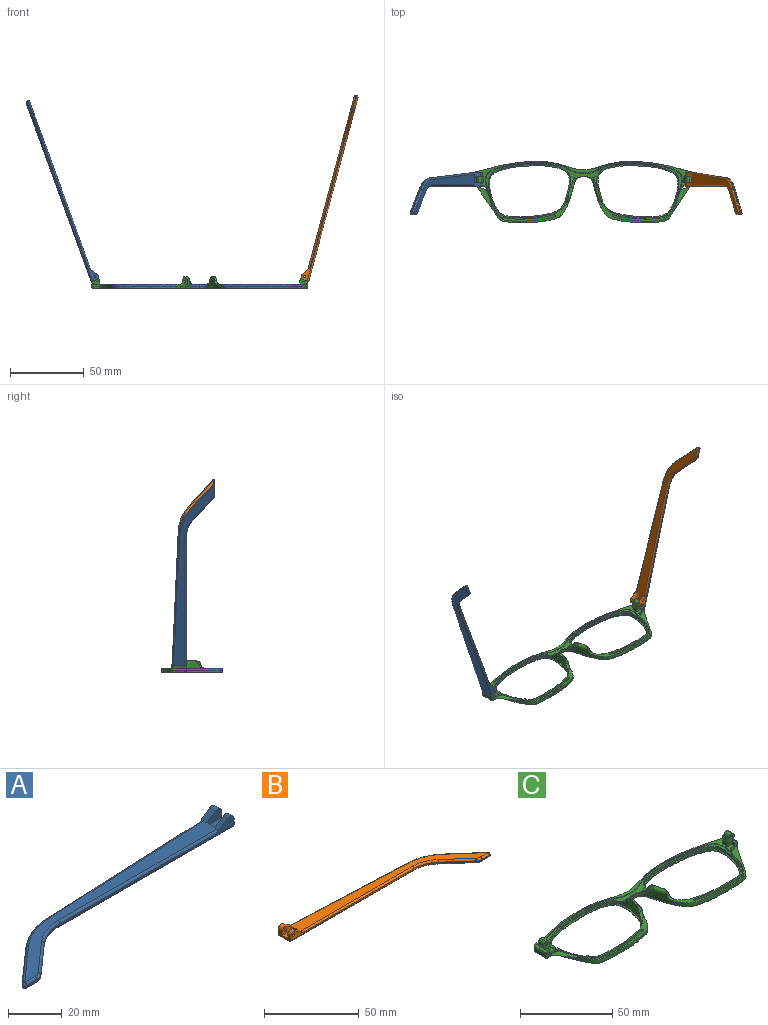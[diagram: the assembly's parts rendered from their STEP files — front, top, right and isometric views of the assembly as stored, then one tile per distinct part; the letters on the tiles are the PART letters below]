
ASSEMBLY  parts=3 mates=2
PART A: 43 faces, bbox 130.2x29.5x5.9 mm
  f0: plane 9.62x3.72mm, normal (1,0,0), area 24.7mm2, adj f1,f3,f4,f5,f10,f16,f18,f28
  f1: cylinder r=2.2mm len=3.45mm, axis (0,-1,0), area 11mm2, adj f0,f2,f4,f37
  f2: plane 6.01x3.91mm, normal (-0.55,0,0.84), area 12.7mm2, adj f1,f4,f9,f19,f37
  f3: plane 2.26x0.1mm, normal (0,0,1), area 0.1mm2, adj f0,f5,f18
  f4: plane 92.1x4.9mm, normal (0,-1,0), area 79.9mm2, adj f0,f1,f2,f14,f19,f36,f42
  f5: plane 93.42x4.13mm, normal (-0.04,1,0), area 64.8mm2, adj f0,f3,f11,f15,f17,f27,f28
  f6: plane 17.82x15.72mm, normal (-0.66,0.75,0), area 14.3mm2, adj f11,f12,f25,f30
  f7: plane 5.46x0.6mm, normal (0,-1,0), area 3.3mm2, adj f12,f13,f23,f32
  f8: plane 14.99x13.23mm, normal (0.66,-0.75,0), area 12mm2, adj f13,f14,f21,f34
  f9: plane 121.18x26.73mm, normal (0,0,1), area 627.7mm2, adj f2,f17,f19,f20,f21,f22,f23,f25
  f10: plane 129.1x27.08mm, normal (0,0,-1), area 686.5mm2, adj f0,f28,f29,f30,f32,f33,f34,f35
  f11: cylinder r=30mm len=18.52mm, axis (0,0,-1), area 12.2mm2, adj f5,f6,f26,f29
  f12: cylinder r=1mm len=1.75mm, axis (0,0,-1), area 1.5mm2, adj f6,f7,f24,f31
  f13: cylinder r=5mm len=3.31mm, axis (0,0,-1), area 2.2mm2, adj f7,f8,f22,f33
  f14: cylinder r=20mm len=13.23mm, axis (0,0,1), area 8.7mm2, adj f4,f8,f20,f35
  f15: plane 5.66x0.25mm, normal (0,0,-1), area 0.7mm2, adj f5,f17,f18
  f16: cylinder r=2.2mm len=3.45mm, axis (0,-1,0), area 14.8mm2, adj f0,f17,f18,f38
  f17: plane 6.01x3.91mm, normal (-0.55,0,0.84), area 16.9mm2, adj f5,f9,f15,f16,f18,f27,f38
  f18: plane 7.92x3.3mm, normal (0,1,0), area 15.9mm2, adj f0,f3,f15,f16,f17,f41
  f19: cylinder r=1mm len=84.18mm, axis (-1,0,0), area 131.4mm2, adj f2,f4,f9,f20
  f20: torus R=21mm, axis (0,0,1), area 23.1mm2, adj f9,f14,f19,f21
  f21: cylinder r=1mm len=15.65mm, axis (-0.75,-0.66,0), area 31.4mm2, adj f8,f9,f20,f22
  f22: torus R=4mm, axis (0,0,1), area 5.3mm2, adj f9,f13,f21,f23
  f23: cylinder r=1mm len=5.46mm, axis (-1,0,0), area 8.6mm2, adj f7,f9,f22,f24
  f24: sphere r=1mm, area 2.4mm2, adj f12,f23,f25
  f25: cylinder r=1mm len=18.48mm, axis (0.75,0.66,0), area 37.3mm2, adj f6,f9,f24,f26
  f26: torus R=29mm, axis (0,0,1), area 31.6mm2, adj f9,f11,f25,f27
  f27: cylinder r=1mm len=85.5mm, axis (1,0.04,0), area 133.5mm2, adj f5,f9,f17,f26
  f28: cylinder r=1mm len=93.46mm, axis (-1,-0.04,0), area 146.9mm2, adj f0,f5,f10,f29
  f29: torus R=29mm, axis (0,0,1), area 31.6mm2, adj f10,f11,f28,f30
  f30: cylinder r=1mm len=18.48mm, axis (-0.75,-0.66,0), area 37.3mm2, adj f6,f10,f29,f31
  f31: sphere r=1mm, area 2.4mm2, adj f12,f30,f32
  f32: cylinder r=1mm len=5.46mm, axis (1,0,0), area 8.6mm2, adj f7,f10,f31,f33
  f33: torus R=4mm, axis (0,0,1), area 5.3mm2, adj f10,f13,f32,f34
  f34: cylinder r=1mm len=15.65mm, axis (0.75,0.66,0), area 31.4mm2, adj f8,f10,f33,f35
  f35: torus R=21mm, axis (0,0,1), area 23.1mm2, adj f10,f14,f34,f36
  f36: cylinder r=1mm len=92.1mm, axis (1,0,0), area 144.7mm2, adj f0,f4,f10,f35
  f37: plane 7.92x4.7mm, normal (0,1,0), area 27mm2, adj f0,f1,f2,f39,f40,f42
  f38: plane 7.92x4.7mm, normal (0,-1,0), area 27mm2, adj f0,f16,f17,f39,f40,f41
  f39: plane 7.92x4.1mm, normal (0,0,1), area 32.5mm2, adj f0,f37,f38,f40
  f40: plane 4.1x1.4mm, normal (1,0,0), area 5.7mm2, adj f9,f37,f38,f39
  f41: cylinder r=0.5mm len=3.1mm, axis (0,-1,0), area 9.7mm2, adj f18,f38
  f42: cylinder r=0.5mm len=2.3mm, axis (0,-1,0), area 7.2mm2, adj f4,f37
PART B: 43 faces, bbox 130.2x29.5x5.9 mm
  f0: plane 9.62x3.72mm, normal (-1,0,0), area 24.7mm2, adj f1,f3,f4,f5,f10,f16,f18,f28
  f1: cylinder r=2.2mm len=3.45mm, axis (0,-1,0), area 11mm2, adj f0,f2,f4,f37
  f2: plane 6.01x3.91mm, normal (0.55,0,0.84), area 12.7mm2, adj f1,f4,f9,f19,f37
  f3: plane 2.26x0.1mm, normal (0,0,1), area 0.1mm2, adj f0,f5,f18
  f4: plane 92.1x4.9mm, normal (0,-1,0), area 78.2mm2, adj f0,f1,f2,f14,f19,f36,f42
  f5: plane 93.42x4.13mm, normal (0.04,1,0), area 64.8mm2, adj f0,f3,f11,f15,f17,f27,f28
  f6: plane 17.82x15.72mm, normal (0.66,0.75,0), area 14.3mm2, adj f11,f12,f25,f30
  f7: plane 5.46x0.6mm, normal (0,-1,0), area 3.3mm2, adj f12,f13,f23,f32
  f8: plane 14.99x13.23mm, normal (-0.66,-0.75,0), area 12mm2, adj f13,f14,f21,f34
  f9: plane 121.18x26.73mm, normal (0,0,1), area 627.7mm2, adj f2,f17,f19,f20,f21,f22,f23,f25
  f10: plane 129.1x27.08mm, normal (0,0,-1), area 686.5mm2, adj f0,f28,f29,f30,f32,f33,f34,f35
  f11: cylinder r=30mm len=18.52mm, axis (0,0,-1), area 12.2mm2, adj f5,f6,f26,f29
  f12: cylinder r=1mm len=1.75mm, axis (0,0,-1), area 1.5mm2, adj f6,f7,f24,f31
  f13: cylinder r=5mm len=3.31mm, axis (0,0,-1), area 2.2mm2, adj f7,f8,f22,f33
  f14: cylinder r=20mm len=13.23mm, axis (0,0,1), area 8.7mm2, adj f4,f8,f20,f35
  f15: plane 5.66x0.25mm, normal (0,0,-1), area 0.7mm2, adj f5,f17,f18
  f16: cylinder r=2.2mm len=3.45mm, axis (0,-1,0), area 14.8mm2, adj f0,f17,f18,f38
  f17: plane 6.01x3.91mm, normal (0.55,0,0.84), area 16.9mm2, adj f5,f9,f15,f16,f18,f27,f38
  f18: plane 7.92x3.3mm, normal (0,1,0), area 14.3mm2, adj f0,f3,f15,f16,f17,f41
  f19: cylinder r=1mm len=84.18mm, axis (1,0,0), area 131.4mm2, adj f2,f4,f9,f20
  f20: torus R=21mm, axis (0,0,1), area 23.1mm2, adj f9,f14,f19,f21
  f21: cylinder r=1mm len=15.65mm, axis (0.75,-0.66,0), area 31.4mm2, adj f8,f9,f20,f22
  f22: torus R=4mm, axis (0,0,1), area 5.3mm2, adj f9,f13,f21,f23
  f23: cylinder r=1mm len=5.46mm, axis (1,0,0), area 8.6mm2, adj f7,f9,f22,f24
  f24: sphere r=1mm, area 2.4mm2, adj f12,f23,f25
  f25: cylinder r=1mm len=18.48mm, axis (-0.75,0.66,0), area 37.3mm2, adj f6,f9,f24,f26
  f26: torus R=29mm, axis (0,0,1), area 31.6mm2, adj f9,f11,f25,f27
  f27: cylinder r=1mm len=85.5mm, axis (-1,0.04,0), area 133.5mm2, adj f5,f9,f17,f26
  f28: cylinder r=1mm len=93.46mm, axis (1,-0.04,0), area 146.9mm2, adj f0,f5,f10,f29
  f29: torus R=29mm, axis (0,0,1), area 31.6mm2, adj f10,f11,f28,f30
  f30: cylinder r=1mm len=18.48mm, axis (0.75,-0.66,0), area 37.3mm2, adj f6,f10,f29,f31
  f31: sphere r=1mm, area 2.4mm2, adj f12,f30,f32
  f32: cylinder r=1mm len=5.46mm, axis (-1,0,0), area 8.6mm2, adj f7,f10,f31,f33
  f33: torus R=4mm, axis (0,0,1), area 5.3mm2, adj f10,f13,f32,f34
  f34: cylinder r=1mm len=15.65mm, axis (-0.75,0.66,0), area 31.4mm2, adj f8,f10,f33,f35
  f35: torus R=21mm, axis (0,0,1), area 23.1mm2, adj f10,f14,f34,f36
  f36: cylinder r=1mm len=92.1mm, axis (-1,0,0), area 144.7mm2, adj f0,f4,f10,f35
  f37: plane 7.92x4.7mm, normal (0,1,0), area 25.4mm2, adj f0,f1,f2,f39,f40,f42
  f38: plane 7.92x4.7mm, normal (0,-1,0), area 25.4mm2, adj f0,f16,f17,f39,f40,f41
  f39: plane 7.92x4.1mm, normal (0,0,1), area 32.5mm2, adj f0,f37,f38,f40
  f40: plane 4.1x1.4mm, normal (-1,0,0), area 5.7mm2, adj f9,f37,f38,f39
  f41: cylinder r=0.88mm len=3.1mm, axis (0,-1,0), area 17mm2, adj f18,f38
  f42: cylinder r=0.88mm len=2.3mm, axis (0,-1,0), area 12.6mm2, adj f4,f37
PART C: 141 faces, bbox 148.1x42.6x10.5 mm
  f0: plane 147.73x42.21mm, normal (0,0,1), area 711.9mm2, adj f4,f5,f6,f7,f8,f12,f20,f23
  f1: bspline ~1.83x1.22mm, area 0.7mm2, adj f2,f7,f37,f52
  f2: bspline ~5.62x4.9mm, area 12.7mm2, adj f1,f7,f37,f41,f43,f52,f53
  f3: plane 4.46x1.43mm, normal (0,0,1), area 0.1mm2, adj f7,f38
  f4: plane 1.23x0.04mm, normal (0,0,1), area 0mm2, adj f0,f7,f22
  f5: plane 6.97x5.07mm, normal (0,1,0), area 22.7mm2, adj f0,f20,f21,f25,f27,f28,f30,f31
  f6: plane 3.2x2.36mm, normal (0,-1,0), area 5.7mm2, adj f0,f20,f26,f29
  f7: extruded ~73.32x41.52mm, area 296.9mm2, adj f0,f1,f2,f3,f4,f8,f13,f14
  f8: extruded ~35.39x5.69mm, area 72.2mm2, adj f0,f7,f18,f79
  f9: plane 144.78x39.54mm, normal (0,0,-1), area 617.6mm2, adj f13,f15,f17,f18,f19,f83,f85,f87
  f10: plane 56.31x36.53mm, normal (0,0,1), area 124.8mm2, adj f11,f19
  f11: extruded ~55.63x36.1mm, area 160.7mm2, adj f10,f12
  f12: extruded ~55.63x36.1mm, area 220.5mm2, adj f0,f11,f39,f40,f41,f42,f43,f44
  f13: bspline ~73.1x32.07mm, area 165.7mm2, adj f7,f9,f14,f83
  f14: bspline ~1x1mm, area 0.8mm2, adj f7,f13,f15
  f15: bspline ~8.99x1.23mm, area 12.6mm2, adj f7,f9,f14,f16
  f16: bspline ~1.04x1mm, area 0.7mm2, adj f7,f15,f17
  f17: bspline ~45.91x8.59mm, area 59.8mm2, adj f7,f9,f16,f18
  f18: bspline ~37.15x6.7mm, area 56.6mm2, adj f8,f9,f17,f88
  f19: bspline ~56.15x36.68mm, area 237.6mm2, adj f9,f10
  f20: plane 4x2.36mm, normal (-1,0,0), area 9.5mm2, adj f0,f5,f6,f21
  f21: plane 4x0.02mm, normal (0.34,0,0.94), area 0.1mm2, adj f5,f20,f28
  f22: plane 2.76x2.53mm, normal (0,-1,0), area 3.9mm2, adj f4,f26,f27,f35,f56
  f23: plane 7.67x1.6mm, normal (0.94,0,-0.34), area 13mm2, adj f0,f35,f36,f56
  f24: plane 2.1x1.69mm, normal (0,1,0), area 2.8mm2, adj f0,f25,f27,f36,f56
  f25: plane 3.3x2.1mm, normal (-1,0,0), area 6.9mm2, adj f0,f5,f24,f27
  f26: plane 2.35x2.1mm, normal (-1,0,0), area 4.9mm2, adj f0,f6,f22,f27,f29
  f27: plane 9.65x1.24mm, normal (0,0,1), area 8.2mm2, adj f5,f22,f24,f25,f26,f29,f30,f56
  f28: plane 4x3.31mm, normal (-0.94,0,0.34), area 14.1mm2, adj f5,f21,f29,f32
  f29: plane 5.77x5.06mm, normal (0,-1,0), area 17mm2, adj f6,f26,f27,f28,f30,f31,f32,f33
  f30: plane 4x2.21mm, normal (0.94,0,-0.34), area 9.4mm2, adj f5,f27,f29,f33
  f31: plane 4x0.01mm, normal (0.34,0,0.94), area 0mm2, adj f5,f29,f32,f33
  f32: cylinder r=1.98mm len=4mm, axis (0,1,0), area 12.4mm2, adj f5,f28,f29,f31
  f33: cylinder r=1.98mm len=4mm, axis (0,-1,0), area 12.4mm2, adj f5,f29,f30,f31
  f34: cylinder r=0.88mm len=4mm, axis (0,-1,0), area 22mm2, adj f5,f29
  f35: cone r=1mm half-angle=20deg, axis (0,0,1), area 2.3mm2, adj f0,f22,f23,f56
  f36: cylinder r=1mm len=2.28mm, axis (-0.34,0,-0.94), area 3mm2, adj f0,f23,f24,f56
  f37: extruded ~3.67x3.11mm, area 5.9mm2, adj f1,f2,f7,f59
  f38: extruded ~4.44x3.37mm, area 15.2mm2, adj f3,f7,f42,f43,f55
  f39: extruded ~4.98x1.36mm, area 6.6mm2, adj f12,f41
  f40: plane 3.51x0.94mm, normal (0,0,1), area 0.3mm2, adj f12,f41,f43
  f41: bspline ~8.14x4.16mm, area 6.4mm2, adj f2,f12,f39,f40,f54
  f42: bspline ~7.26x7.26mm, area 6.6mm2, adj f12,f38,f43,f55
  f43: bspline ~11x5.07mm, area 21.4mm2, adj f2,f7,f12,f38,f40,f42
  f44: plane 2.88x1.51mm, normal (0,0,-1), area 1.8mm2, adj f12,f45
  f45: cylinder r=2.28mm len=2.86mm, axis (0,0,1), area 1.8mm2, adj f0,f12,f44,f54
  f46: plane 2.5x1.83mm, normal (0,0,-1), area 1.7mm2, adj f12,f47
  f47: cylinder r=2.28mm len=2.47mm, axis (0,0,1), area 1.7mm2, adj f0,f12,f46
  f48: plane 1.79x1.31mm, normal (0,0,-1), area 0.9mm2, adj f12,f49
  f49: cylinder r=1.3mm len=1.78mm, axis (0,0,1), area 1.3mm2, adj f0,f12,f48
  f50: plane 1.95x1.68mm, normal (0,0,-1), area 1.5mm2, adj f12,f51
  f51: cylinder r=1.3mm len=1.93mm, axis (0,0,1), area 1.5mm2, adj f0,f12,f50
  f52: bspline ~2.66x2.04mm, area 1.9mm2, adj f1,f2,f7,f53,f58
  f53: bspline ~3.55x3.47mm, area 3.7mm2, adj f0,f2,f52,f54,f58
  f54: bspline ~6.16x4.45mm, area 7.6mm2, adj f0,f12,f41,f45,f53
  f55: bspline ~3.72x3.66mm, area 7.7mm2, adj f0,f7,f12,f38,f42
  f56: plane 9.71x1.44mm, normal (0.34,0,0.94), area 13.9mm2, adj f22,f23,f24,f27,f35,f36
  f57: bspline ~6.39x2.13mm, area 2.6mm2, adj f0,f7,f58,f127
  f58: bspline ~2.1x1.46mm, area 0.6mm2, adj f7,f52,f53,f57
  f59: bspline ~5.25x1.76mm, area 0mm2, adj f7,f37
  f60: extruded ~66.46x12.39mm, area 109.6mm2, adj f0,f61,f71,f130
  f61: extruded ~24.66x11.21mm, area 41.6mm2, adj f0,f60,f62,f71
  f62: cylinder r=0.75mm len=1.5mm, axis (0,0,1), area 1mm2, adj f0,f61,f63,f71
  f63: extruded ~34.22x2.89mm, area 51.8mm2, adj f0,f62,f64,f71
  f64: cylinder r=0.75mm len=1.5mm, axis (0,0,1), area 3.5mm2, adj f0,f63,f65,f71
  f65: extruded ~35.01x2.95mm, area 53mm2, adj f0,f64,f66,f71
  f66: cylinder r=0.75mm len=1.5mm, axis (0,0,1), area 1.8mm2, adj f0,f65,f67,f71
  f67: extruded ~25x11.43mm, area 42.2mm2, adj f0,f66,f68,f71
  f68: cylinder r=0.25mm len=1.5mm, axis (0,0,1), area 0.1mm2, adj f0,f67,f69,f71
  f69: extruded ~66.94x12.89mm, area 110.7mm2, adj f0,f68,f70,f71
  f70: plane 1.5x0.25mm, normal (1,-0.09,0), area 0.4mm2, adj f0,f69,f71,f140
  f71: plane 133.92x40.04mm, normal (0,0,1), area 209.8mm2, adj f60,f61,f62,f63,f64,f65,f66,f67
  f72: bspline ~2.22x1.4mm, area 0.7mm2, adj f73,f78,f107,f122
  f73: bspline ~5.62x4.9mm, area 12.6mm2, adj f72,f78,f107,f111,f113,f122,f123
  f74: plane 4.46x1.43mm, normal (0,0,1), area 0.1mm2, adj f78,f108
  f75: plane 1.23x0.04mm, normal (0,0,1), area 0mm2, adj f0,f78,f92
  f76: plane 6.97x5.07mm, normal (0,1,0), area 22.7mm2, adj f0,f90,f91,f95,f97,f98,f100,f101
  f77: plane 3.2x2.36mm, normal (0,-1,0), area 5.7mm2, adj f0,f90,f96,f99
  f78: extruded ~73.32x41.52mm, area 296.9mm2, adj f0,f7,f72,f73,f74,f75,f79,f83
  f79: extruded ~35.39x5.69mm, area 72.2mm2, adj f0,f8,f78,f88
  f80: plane 56.31x36.53mm, normal (0,0,1), area 124.8mm2, adj f81,f89
  f81: extruded ~55.63x36.1mm, area 160.7mm2, adj f80,f82
  f82: extruded ~55.63x36.1mm, area 220.5mm2, adj f0,f81,f109,f110,f111,f112,f113,f114
  f83: bspline ~73.1x32.07mm, area 165.7mm2, adj f9,f13,f78,f84
  f84: bspline ~1x1mm, area 0.8mm2, adj f78,f83,f85
  f85: bspline ~8.99x1.23mm, area 12.6mm2, adj f9,f78,f84,f86
  f86: bspline ~1.04x1mm, area 0.8mm2, adj f78,f85,f87
  f87: bspline ~45.91x8.59mm, area 59.8mm2, adj f9,f78,f86,f88
  f88: bspline ~37.15x6.7mm, area 56.6mm2, adj f9,f18,f79,f87
  f89: bspline ~56.15x36.68mm, area 237.6mm2, adj f9,f80
  f90: plane 4x2.36mm, normal (1,0,0), area 9.5mm2, adj f0,f76,f77,f91
  f91: plane 4x0.02mm, normal (-0.34,0,0.94), area 0.1mm2, adj f76,f90,f98
  f92: plane 2.76x2.53mm, normal (0,-1,0), area 3.9mm2, adj f75,f96,f97,f105,f126
  f93: plane 7.67x1.6mm, normal (-0.94,0,-0.34), area 13mm2, adj f0,f105,f106,f126
  f94: plane 2.1x1.69mm, normal (0,1,0), area 2.8mm2, adj f0,f95,f97,f106,f126
  f95: plane 3.3x2.1mm, normal (1,0,0), area 6.9mm2, adj f0,f76,f94,f97
  f96: plane 2.35x2.1mm, normal (1,0,0), area 4.9mm2, adj f0,f77,f92,f97,f99
  f97: plane 9.65x1.24mm, normal (0,0,1), area 8.2mm2, adj f76,f92,f94,f95,f96,f99,f100,f126
  f98: plane 4x3.31mm, normal (0.94,0,0.34), area 14.1mm2, adj f76,f91,f99,f102
  f99: plane 5.77x5.06mm, normal (0,-1,0), area 17mm2, adj f77,f96,f97,f98,f100,f101,f102,f103
  f100: plane 4x2.21mm, normal (-0.94,0,-0.34), area 9.4mm2, adj f76,f97,f99,f103
  f101: plane 4x0.01mm, normal (-0.34,0,0.94), area 0mm2, adj f76,f99,f102,f103
  f102: cylinder r=1.98mm len=4mm, axis (0,1,0), area 12.4mm2, adj f76,f98,f99,f101
  f103: cylinder r=1.98mm len=4mm, axis (0,-1,0), area 12.4mm2, adj f76,f99,f100,f101
  f104: cylinder r=0.88mm len=4mm, axis (0,-1,0), area 22mm2, adj f76,f99
  f105: cone r=1mm half-angle=20deg, axis (0,0,1), area 2.3mm2, adj f0,f92,f93,f126
  f106: cylinder r=1mm len=2.28mm, axis (0.34,0,-0.94), area 3mm2, adj f0,f93,f94,f126
  f107: extruded ~3.67x3.11mm, area 5.9mm2, adj f72,f73,f78,f129
  f108: extruded ~4.44x3.37mm, area 15.2mm2, adj f74,f78,f112,f113,f125
  f109: extruded ~4.98x1.36mm, area 6.6mm2, adj f82,f111
  f110: plane 3.51x0.94mm, normal (0,0,1), area 0.3mm2, adj f82,f111,f113
  f111: bspline ~8.14x4.16mm, area 6.4mm2, adj f73,f82,f109,f110,f124
  f112: bspline ~7.26x7.26mm, area 6.6mm2, adj f82,f108,f113,f125
  f113: bspline ~11x5.07mm, area 21.4mm2, adj f73,f78,f82,f108,f110,f112
  f114: plane 2.88x1.51mm, normal (0,0,-1), area 1.8mm2, adj f82,f115
  f115: cylinder r=2.28mm len=2.86mm, axis (0,0,1), area 1.8mm2, adj f0,f82,f114,f124
  f116: plane 2.5x1.83mm, normal (0,0,-1), area 1.7mm2, adj f82,f117
  f117: cylinder r=2.28mm len=2.47mm, axis (0,0,1), area 1.7mm2, adj f0,f82,f116
  f118: plane 1.79x1.31mm, normal (0,0,-1), area 0.9mm2, adj f82,f119
  f119: cylinder r=1.3mm len=1.78mm, axis (0,0,1), area 1.3mm2, adj f0,f82,f118
  f120: plane 1.95x1.68mm, normal (0,0,-1), area 1.5mm2, adj f82,f121
  f121: cylinder r=1.3mm len=1.93mm, axis (0,0,1), area 1.5mm2, adj f0,f82,f120
  f122: bspline ~2.65x2.03mm, area 1.9mm2, adj f72,f73,f78,f123,f128
  f123: bspline ~3.55x3.47mm, area 3.7mm2, adj f0,f73,f122,f124,f128
  f124: bspline ~5.94x4.42mm, area 7.6mm2, adj f0,f82,f111,f115,f123
  f125: bspline ~3.72x3.66mm, area 7.7mm2, adj f0,f78,f82,f108,f112
  f126: plane 9.71x1.44mm, normal (-0.34,0,0.94), area 13.9mm2, adj f92,f93,f94,f97,f105,f106
  f127: bspline ~6.39x2.13mm, area 2.6mm2, adj f0,f57,f78,f128
  f128: bspline ~1.82x1.13mm, area 0.6mm2, adj f78,f122,f123,f127
  f129: bspline ~5.25x1.76mm, area 0mm2, adj f78,f107
  f130: extruded ~66.46x12.39mm, area 109.6mm2, adj f0,f60,f71,f131
  f131: extruded ~24.66x11.21mm, area 41.6mm2, adj f0,f71,f130,f132
  f132: cylinder r=0.75mm len=1.5mm, axis (0,0,1), area 1mm2, adj f0,f71,f131,f133
  f133: extruded ~34.22x2.89mm, area 51.8mm2, adj f0,f71,f132,f134
  f134: cylinder r=0.75mm len=1.5mm, axis (0,0,1), area 3.5mm2, adj f0,f71,f133,f135
  f135: extruded ~35.01x2.95mm, area 53mm2, adj f0,f71,f134,f136
  f136: cylinder r=0.75mm len=1.5mm, axis (0,0,1), area 1.8mm2, adj f0,f71,f135,f137
  f137: extruded ~25x11.43mm, area 42.2mm2, adj f0,f71,f136,f138
  f138: cylinder r=0.25mm len=1.5mm, axis (0,0,1), area 0.1mm2, adj f0,f71,f137,f139
  f139: extruded ~66.94x12.89mm, area 110.7mm2, adj f0,f71,f138,f140
  f140: plane 1.5x0.25mm, normal (-1,-0.09,0), area 0.4mm2, adj f0,f70,f71,f139
PLACE A rot(axis=(0,1,0),70deg) t=(-84.77,-5.75,56)mm
PLACE B rot(axis=(0,-1,0),75deg) t=(68.2,-5.75,-61.61)mm
PLACE C t=(10.15,-1.13,-5.77)mm
MATE revolute A.f1 <-> C.f102  axis (0,-1,0) through (-60.89,2.72,1.22)mm
MATE revolute B.f41 <-> C.f33  axis (0,-1,0) through (81.2,2.72,1.21)mm
